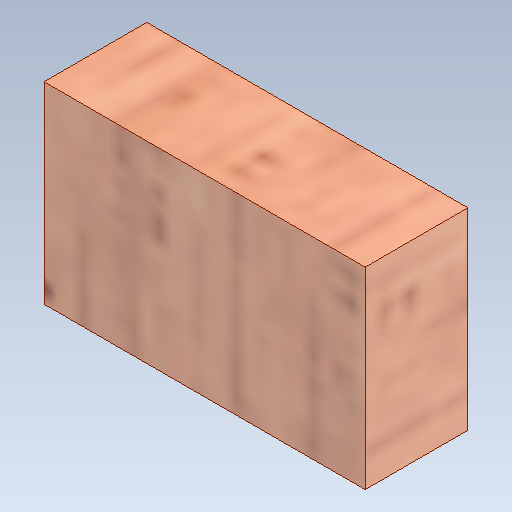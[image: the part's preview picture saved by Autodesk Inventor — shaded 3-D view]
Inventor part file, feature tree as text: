
AUTODESK INVENTOR PART (.ipt)
format: ipt  version: 2020 (Build 240168000, 168)  size: 178,176 bytes
history: native  units: mm
features: extrude x1, sketch x1
ambient origin geometry x8: Origin, YZ Plane, XZ Plane, XY Plane, X Axis, Y Axis, Z Axis, Center Point
bodies: Solid1 (feature_tree)
feature tree (2):
  extrude  "Extrusion1"  Depth=25.0mm
  sketch  "Sketch1"  dims[d0=15.0mm d1=25.0mm d2=8.0mm d3=0.0mm]
